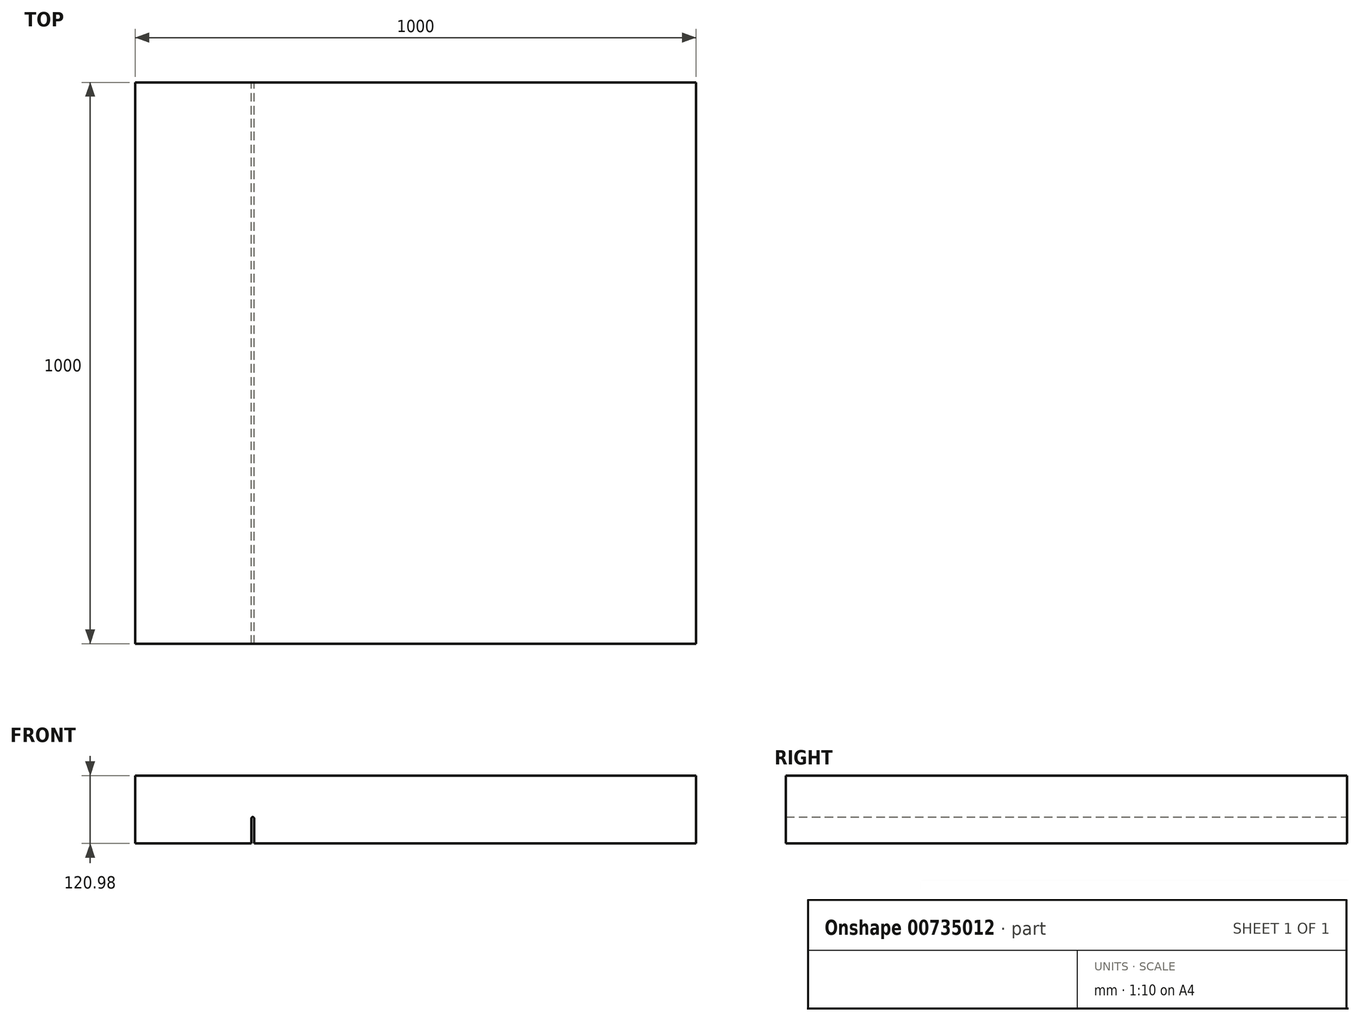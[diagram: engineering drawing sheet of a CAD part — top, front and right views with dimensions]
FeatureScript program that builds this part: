
annotation { "Feature Type Name" : "Feature", "Feature Type Description" : "" }
export const myFeature = defineFeature(function(context is Context, id is Id, definition is map)
    precondition{}
    {
        {
            var Q0;
            Q0=qCreatedBy(makeId("Front.planeOp"),FACE);
            var sketch = newSketch(context, id + "F0", { "sketchPlane" : qUnion([Q0])});
            skLineSegment(sketch, "E0.bottom", {"start": v(-207.26, 0) * mm, "end": v(792.74, 0) * mm});
            skLineSegment(sketch, "E0.top", {"start": v(-207.26, 120.98) * mm, "end": v(792.74, 120.98) * mm});
            skLineSegment(sketch, "E0.left", {"start": v(-207.26, 0) * mm, "end": v(-207.26, 120.98) * mm});
            skLineSegment(sketch, "E0.right", {"start": v(792.74, 0) * mm, "end": v(792.74, 120.98) * mm});
            skSolve(sketch);
        }
        {
            var Q0;
            Q0=qCreatedBy(makeId("Front.planeOp"),FACE);
            var sketch = newSketch(context, id + "F1", { "sketchPlane" : qUnion([Q0])});
            skLineSegment(sketch, "E1.bottom", {"start": v(4.91, 0) * mm, "end": v(0, 0) * mm});
            skLineSegment(sketch, "E1.top", {"start": v(4.91, 44.66) * mm, "end": v(0, 44.66) * mm});
            skLineSegment(sketch, "E1.left", {"start": v(4.91, 0) * mm, "end": v(4.91, 44.66) * mm});
            skLineSegment(sketch, "E1.right", {"start": v(0, 0) * mm, "end": v(0, 44.66) * mm});
            skArc(sketch, "E2", {"start": v(4.91, 44.66) * mm, "mid": v(2.46, 47.12) * mm, "end": v(0, 44.66) * mm});
            skSolve(sketch);
        }
        {
            var Q0;
            Q0 = qSketchRegion(id + "F0", true);
            extrude(context, id + "F2", {"entities" : qUnion([Q0]), "depth" : 1000 * mm, "offsetDistance" : 25 * mm});
        }
        {
            var Q0;
            Q0 = qSketchRegion(id + "F1", true);
            extrude(context, id + "F3", {"entities" : qUnion([Q0]), "operationType" : NewBodyOperationType.REMOVE, "depth" : 1000 * mm, "offsetDistance" : 25 * mm});
        }
    });
